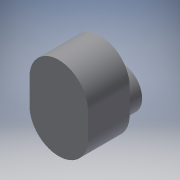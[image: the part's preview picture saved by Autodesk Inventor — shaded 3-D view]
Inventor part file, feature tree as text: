
AUTODESK INVENTOR PART (.ipt)
format: ipt  version: 2017 (Build 210142000, 142)  size: 110,592 bytes
history: native  units: mm
features: extrude x2, sketch x2, projected_geometry x1
ambient origin geometry x8: Origin, YZ Plane, XZ Plane, XY Plane, X Axis, Y Axis, Z Axis, Center Point
bodies: Solid1 (feature_tree)
feature tree (5):
  extrude  "Extrusion1"  Depth=70.0mm
  extrude  "Extrusion2"  Depth=100.0mm
  sketch  "Sketch1"  dims[d0=60.0mm d1=70.0mm]
  sketch  "Sketch2"  dims[d2=100.0mm d3=0.0mm d4=100.0mm d5=50.0mm d6=0.0mm]
  projected_geometry  "Projected Loop1"
